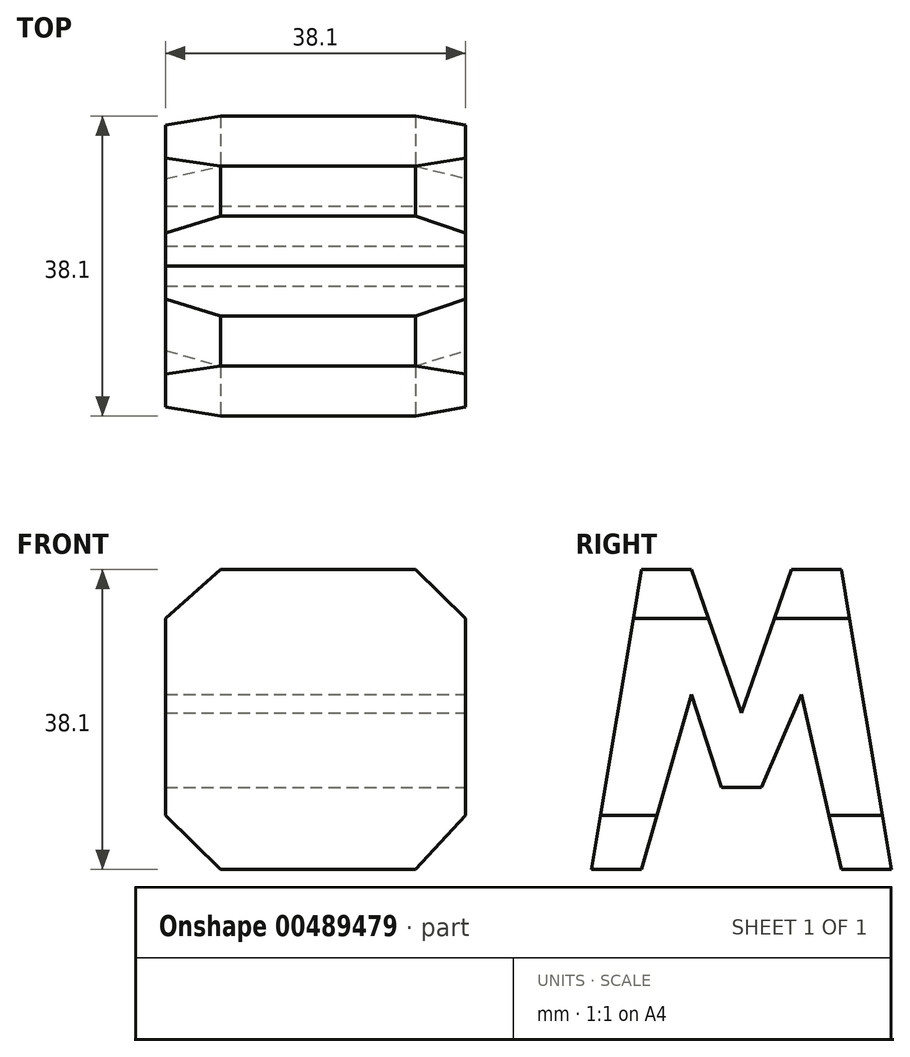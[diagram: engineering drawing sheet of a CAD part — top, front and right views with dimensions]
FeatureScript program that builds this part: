
annotation { "Feature Type Name" : "Feature", "Feature Type Description" : "" }
export const myFeature = defineFeature(function(context is Context, id is Id, definition is map)
    precondition{}
    {
        {
            var Q0;
            Q0=qCreatedBy(makeId("Front.planeOp"),FACE);
            var sketch = newSketch(context, id + "F0", { "sketchPlane" : qUnion([Q0])});
            skLineSegment(sketch, "E0", {"start": v(0, 0) * mm, "end": v(0, 38.1) * mm});
            skLineSegment(sketch, "E1", {"start": v(0, 38.1) * mm, "end": v(38.1, 38.1) * mm});
            skLineSegment(sketch, "E2", {"start": v(38.1, 38.1) * mm, "end": v(38.1, 0) * mm});
            skLineSegment(sketch, "E3", {"start": v(38.1, 0) * mm, "end": v(0, 0) * mm});
            skSolve(sketch);
        }
        {
            var Q0;
            Q0 = qSketchRegion(id + "F0", true);
            extrude(context, id + "F1", {"entities" : qUnion([Q0]), "depth" : 38.1 * mm, "offsetDistance" : 25.4 * mm});
        }
        {
            var Q0;
            Q0=qCreatedBy(makeId("Front.planeOp"),FACE);
            cPlane(context, id + "F2", {"entities" : qUnion([Q0]), "cplaneType" : CPlaneType.OFFSET, "offset" : 38.1 * mm, "width" : 152.4 * mm, "height" : 152.4 * mm});
        }
        {
            var Q0;
            Q0=qCreatedBy(makeId("Right.planeOp"),FACE);
            cPlane(context, id + "F3", {"entities" : qUnion([Q0]), "cplaneType" : CPlaneType.OFFSET, "offset" : 38.1 * mm, "width" : 152.4 * mm, "height" : 152.4 * mm});
        }
        {
            var Q0;
            Q0=qCreatedBy(id+"F3.planeOp",FACE);
            var sketch = newSketch(context, id + "F4", { "sketchPlane" : qUnion([Q0])});
            skLineSegment(sketch, "E4", {"start": v(0, 0) * mm, "end": v(0, 38.1) * mm});
            skLineSegment(sketch, "E5", {"start": v(0, 38.1) * mm, "end": v(-38.1, 38.1) * mm});
            skLineSegment(sketch, "E6", {"start": v(-38.1, 38.1) * mm, "end": v(-38.1, 0) * mm});
            skLineSegment(sketch, "E7", {"start": v(-38.1, 0) * mm, "end": v(0, 0) * mm});
            skLineSegment(sketch, "E8", {"start": v(-31.75, 38.1) * mm, "end": v(-25.4, 38.1) * mm});
            skLineSegment(sketch, "E9", {"start": v(-25.4, 38.1) * mm, "end": v(-19.05, 19.88) * mm});
            skLineSegment(sketch, "E10", {"start": v(-19.05, 19.88) * mm, "end": v(-12.7, 38.1) * mm});
            skLineSegment(sketch, "E11", {"start": v(-12.7, 38.1) * mm, "end": v(-6.35, 38.1) * mm});
            skLineSegment(sketch, "E12", {"start": v(-6.35, 38.1) * mm, "end": v(0, 0) * mm});
            skLineSegment(sketch, "E13", {"start": v(-25.4, 22.23) * mm, "end": v(-31.75, 0) * mm});
            skLineSegment(sketch, "E14", {"start": v(-31.75, 0) * mm, "end": v(-36.31, 0) * mm});
            skLineSegment(sketch, "E15", {"start": v(-25.4, 22.23) * mm, "end": v(-21.6, 10.45) * mm});
            skLineSegment(sketch, "E16", {"start": v(-21.6, 10.45) * mm, "end": v(-16.51, 10.45) * mm});
            skLineSegment(sketch, "E17", {"start": v(-16.51, 10.45) * mm, "end": v(-11.43, 22.22) * mm});
            skLineSegment(sketch, "E18", {"start": v(-31.75, 38.1) * mm, "end": v(-38.1, 0) * mm});
            skPoint(sketch, "E19.start.orphan", {"position": v(-36.31, 0) * mm});
            skLineSegment(sketch, "E20", {"start": v(-11.43, 22.22) * mm, "end": v(-6.35, 0) * mm});
            skSolve(sketch);
        }
        {
            var Q0;
            {var subQ0=sQuery(id+"F4.wireOp",EDGE,"E6");Q0=makeQuery(id+"F4.imprint","IMPRINT",FACE,{"disambiguationData":[TD([[makeQuery(id+"F4.imprint","IMPRINT",EDGE,{"derivedFrom":subQ0}),1.0]])]});}
            var Q1;
            {var subQ0=sQuery(id+"F4.wireOp",EDGE,"E9");Q1=makeQuery(id+"F4.imprint","IMPRINT",FACE,{"disambiguationData":[TD([[makeQuery(id+"F4.imprint","IMPRINT",EDGE,{"derivedFrom":subQ0}),1.0]])]});}
            var Q2;
            {var subQ0=sQuery(id+"F4.wireOp",EDGE,"E4");Q2=makeQuery(id+"F4.imprint","IMPRINT",FACE,{"disambiguationData":[TD([[makeQuery(id+"F4.imprint","IMPRINT",EDGE,{"derivedFrom":subQ0}),1.0]])]});}
            var Q3;
            {var subQ0=sQuery(id+"F4.wireOp",EDGE,"E13");Q3=makeQuery(id+"F4.imprint","IMPRINT",FACE,{"disambiguationData":[TD([[makeQuery(id+"F4.imprint","IMPRINT",EDGE,{"derivedFrom":subQ0}),1.0]])]});}
            extrude(context, id + "F5", {"entities" : qUnion([Q0, Q1, Q2, Q3]), "operationType" : NewBodyOperationType.REMOVE, "oppositeDirection" : true, "depth" : 38.1 * mm, "offsetDistance" : 25.4 * mm});
        }
        {
            var Q0;
            Q0=qCreatedBy(id+"F2.planeOp",FACE);
            var sketch = newSketch(context, id + "F6", { "sketchPlane" : qUnion([Q0])});
            skLineSegment(sketch, "E21", {"start": v(0, 0) * mm, "end": v(0, 38.1) * mm});
            skLineSegment(sketch, "E22", {"start": v(0, 38.1) * mm, "end": v(38.1, 38.1) * mm});
            skLineSegment(sketch, "E23", {"start": v(38.1, 38.1) * mm, "end": v(38.1, 0) * mm});
            skLineSegment(sketch, "E24", {"start": v(38.1, 0) * mm, "end": v(0, 0) * mm});
            skLineSegment(sketch, "E25", {"start": v(38.1, 12.49) * mm, "end": v(38.1, 26.25) * mm});
            skLineSegment(sketch, "E26", {"start": v(38.1, 31.85) * mm, "end": v(31.72, 38.1) * mm});
            skLineSegment(sketch, "E27", {"start": v(31.72, 38.1) * mm, "end": v(7, 38.1) * mm});
            skLineSegment(sketch, "E28", {"start": v(7, 38.1) * mm, "end": v(0, 31.85) * mm});
            skLineSegment(sketch, "E29", {"start": v(0, 31.85) * mm, "end": v(0, 6.88) * mm});
            skLineSegment(sketch, "E30", {"start": v(0, 6.88) * mm, "end": v(7, 0) * mm});
            skLineSegment(sketch, "E31", {"start": v(7, 0) * mm, "end": v(31.72, 0) * mm});
            skLineSegment(sketch, "E32", {"start": v(31.72, 0) * mm, "end": v(38.1, 6.88) * mm});
            skLineSegment(sketch, "E33", {"start": v(38.1, 6.88) * mm, "end": v(38.1, 12.49) * mm});
            skPoint(sketch, "E34.end.orphan", {"position": v(31.72, 31.85) * mm});
            skPoint(sketch, "E35.start.orphan", {"position": v(31.72, 6.88) * mm});
            skPoint(sketch, "E36.end.orphan", {"position": v(7, 6.88) * mm});
            skPoint(sketch, "E36.start.orphan", {"position": v(7, 31.85) * mm});
            skPoint(sketch, "E37.end.orphan", {"position": v(31.72, 26.25) * mm});
            skLineSegment(sketch, "E38", {"start": v(31.72, 26.25) * mm, "end": v(31.72, 31.85) * mm});
            skLineSegment(sketch, "E39", {"start": v(31.72, 6.88) * mm, "end": v(31.72, 12.49) * mm});
            skLineSegment(sketch, "E40", {"start": v(31.72, 12.49) * mm, "end": v(38.1, 12.49) * mm});
            skLineSegment(sketch, "E41", {"start": v(38.1, 26.25) * mm, "end": v(31.72, 26.25) * mm});
            skLineSegment(sketch, "E42", {"start": v(31.72, 6.88) * mm, "end": v(10.83, 6.88) * mm});
            skLineSegment(sketch, "E43", {"start": v(10.83, 6.88) * mm, "end": v(7, 10.42) * mm});
            skLineSegment(sketch, "E44", {"start": v(7, 10.42) * mm, "end": v(7, 27) * mm});
            skLineSegment(sketch, "E45", {"start": v(7, 27) * mm, "end": v(11.7, 32.07) * mm});
            skLineSegment(sketch, "E46", {"start": v(11.7, 32.07) * mm, "end": v(31.72, 31.85) * mm});
            skSolve(sketch);
        }
        {
            var Q0;
            {var subQ3=sQuery(id+"F6.wireOp",EDGE,"E28");Q0=makeQuery(id+"F6.imprint","IMPRINT",FACE,{"disambiguationData":[TD([[makeQuery(id+"F6.imprint","IMPRINT",EDGE,{"derivedFrom":subQ3}),-1.0]])]});}
            var Q1;
            {var subQ3=sQuery(id+"F6.wireOp",EDGE,"E30");Q1=makeQuery(id+"F6.imprint","IMPRINT",FACE,{"disambiguationData":[TD([[makeQuery(id+"F6.imprint","IMPRINT",EDGE,{"derivedFrom":subQ3}),-1.0]])]});}
            var Q2;
            {var subQ3=sQuery(id+"F6.wireOp",EDGE,"E26");Q2=makeQuery(id+"F6.imprint","IMPRINT",FACE,{"disambiguationData":[TD([[makeQuery(id+"F6.imprint","IMPRINT",EDGE,{"derivedFrom":subQ3}),-1.0]])]});}
            var Q3;
            {var subQ3=sQuery(id+"F6.wireOp",EDGE,"E32");Q3=makeQuery(id+"F6.imprint","IMPRINT",FACE,{"disambiguationData":[TD([[makeQuery(id+"F6.imprint","IMPRINT",EDGE,{"derivedFrom":subQ3}),-1.0]])]});}
            var Q4;
            Q4=makeQuery(id+"F6.imprint","IMPRINT",FACE,{"disambiguationData":[TD([[makeQuery(id+"F6.imprint","IMPRINT",EDGE,{"derivedFrom":sQuery(id+"F6.wireOp",EDGE,"E25")}),1.0]])]});
            extrude(context, id + "F7", {"entities" : qUnion([Q0, Q1, Q2, Q3, Q4]), "operationType" : NewBodyOperationType.REMOVE, "oppositeDirection" : true, "depth" : 38.1 * mm, "offsetDistance" : 25.4 * mm});
        }
    });
